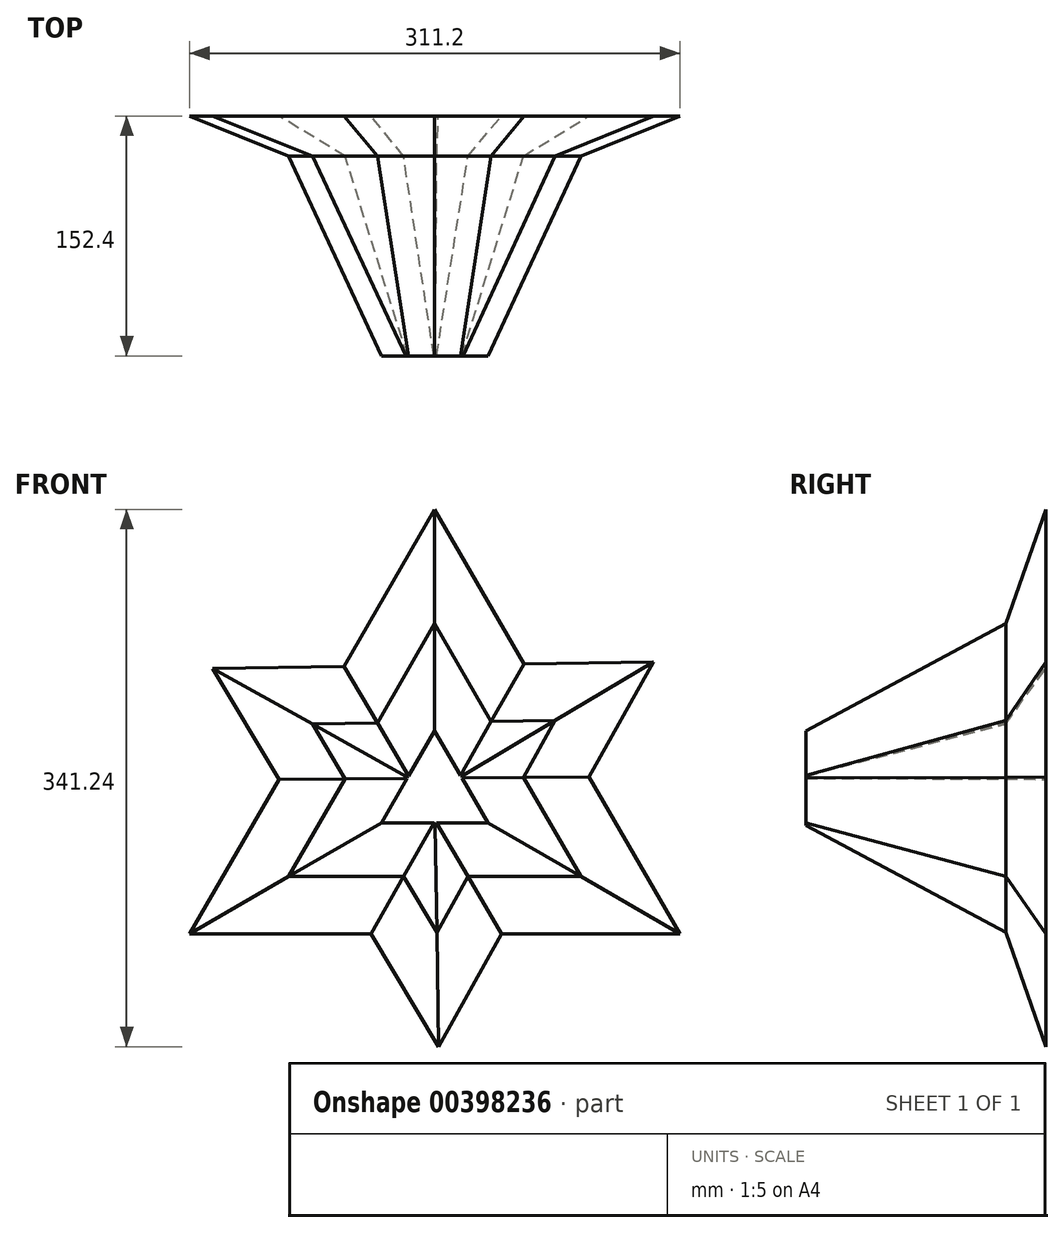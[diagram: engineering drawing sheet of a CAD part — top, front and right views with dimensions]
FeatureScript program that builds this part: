
annotation { "Feature Type Name" : "Feature", "Feature Type Description" : "" }
export const myFeature = defineFeature(function(context is Context, id is Id, definition is map)
    precondition{}
    {
        {
            var Q0;
            Q0=qCreatedBy(makeId("Front.planeOp"),FACE);
            cPlane(context, id + "F0", {"entities" : qUnion([Q0]), "cplaneType" : CPlaneType.OFFSET, "offset" : 46.48 * mm, "width" : 152.4 * mm, "height" : 152.4 * mm});
        }
        {
            var Q0;
            Q0=qCreatedBy(makeId("Front.planeOp"),FACE);
            var sketch = newSketch(context, id + "F1", { "sketchPlane" : qUnion([Q0])});
            skCircle(sketch, "E0.cCircle", {"center": v(0, 0) * mm, "radius": 44.52 * mm, "construction": true});
            skLineSegment(sketch, "E0.0", {"start": v(1.28, -89.03) * mm, "end": v(-77.74, 43.4) * mm});
            skLineSegment(sketch, "E0.1", {"start": v(-77.74, 43.4) * mm, "end": v(76.46, 45.62) * mm});
            skLineSegment(sketch, "E0.2", {"start": v(76.46, 45.62) * mm, "end": v(1.28, -89.03) * mm});
            skPoint(sketch, "E0.0.midPoint", {"position": v(-38.23, -22.81) * mm});
            skCircle(sketch, "E1.cCircle", {"center": v(0, 0) * mm, "radius": 53.56 * mm, "construction": true});
            skLineSegment(sketch, "E1.0", {"start": v(92.77, -53.56) * mm, "end": v(-92.77, -53.56) * mm});
            skLineSegment(sketch, "E1.1", {"start": v(-92.77, -53.56) * mm, "end": v(0, 107.12) * mm});
            skLineSegment(sketch, "E1.2", {"start": v(0, 107.12) * mm, "end": v(92.77, -53.56) * mm});
            skPoint(sketch, "E1.0.midPoint", {"position": v(0, -53.56) * mm});
            skSolve(sketch);
        }
        {
            var Q0;
            Q0 = qSketchRegion(id + "F1", true);
            extrude(context, id + "F2", {"entities" : qUnion([Q0]), "depth" : 127 * mm, "hasDraft" : true, "draftAngle" : 15 * degree, "draftPullDirection" : true, "hasSecondDirection" : true, "secondDirectionOppositeDirection" : true, "secondDirectionDepth" : 25.4 * mm, "hasSecondDirectionDraft" : true, "secondDirectionDraftAngle" : 55 * degree});
        }
    });
